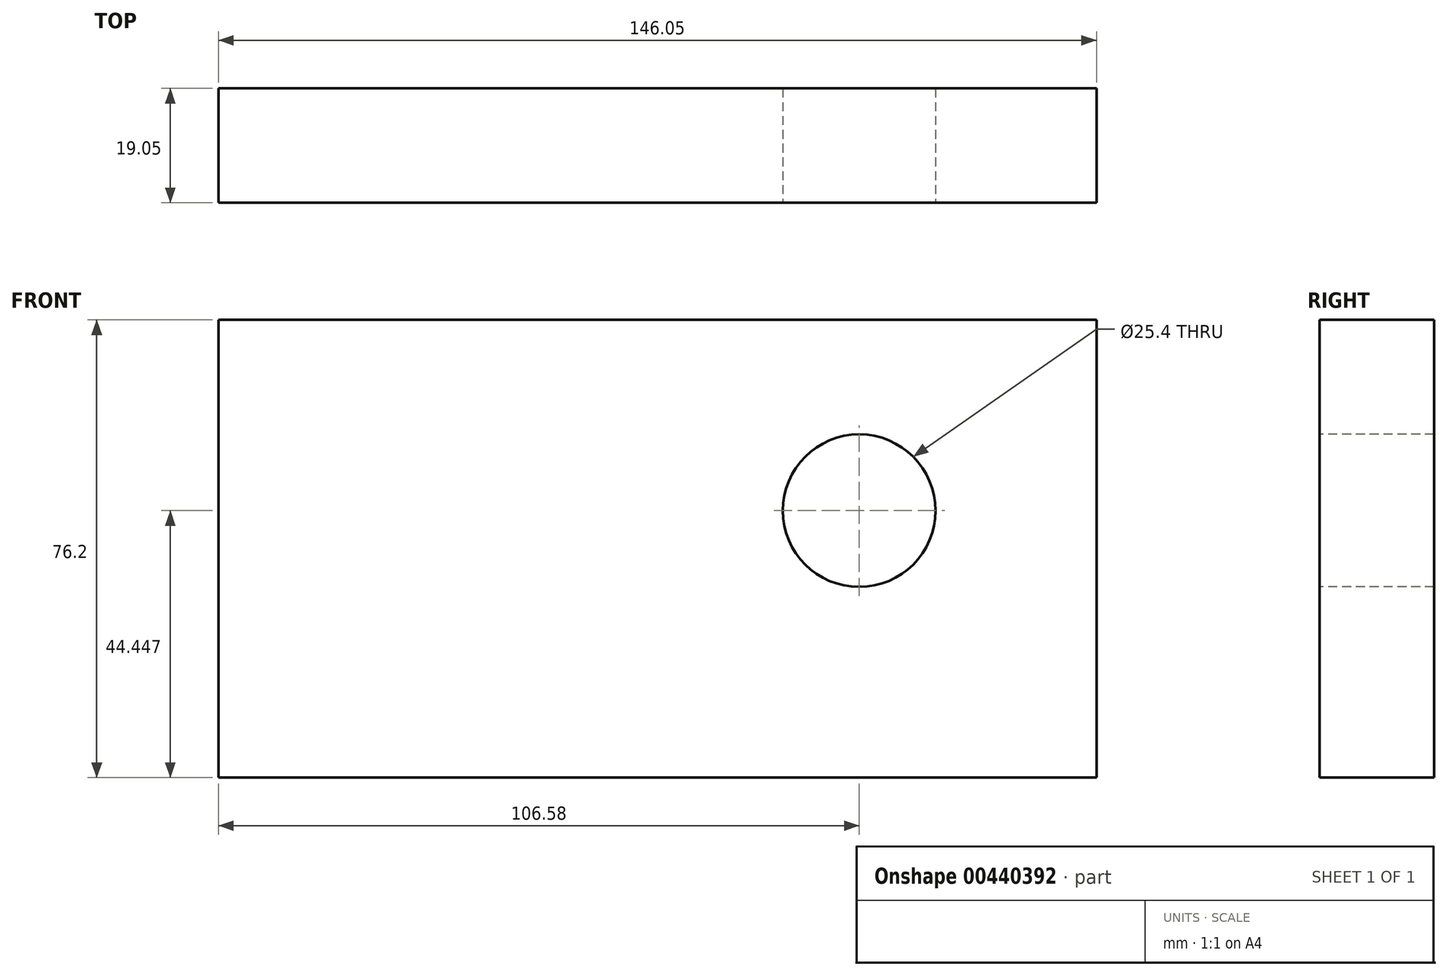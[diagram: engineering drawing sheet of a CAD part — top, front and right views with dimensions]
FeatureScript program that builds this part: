
annotation { "Feature Type Name" : "Feature", "Feature Type Description" : "" }
export const myFeature = defineFeature(function(context is Context, id is Id, definition is map)
    precondition{}
    {
        {
            var Q0;
            Q0=qCreatedBy(makeId("Front.planeOp"),FACE);
            var sketch = newSketch(context, id + "F0", { "sketchPlane" : qUnion([Q0])});
            skLineSegment(sketch, "E0.bottom", {"start": v(-106.58, 69.18) * mm, "end": v(39.47, 69.18) * mm});
            skLineSegment(sketch, "E0.top", {"start": v(-106.58, -7.02) * mm, "end": v(39.47, -7.02) * mm});
            skLineSegment(sketch, "E0.left", {"start": v(-106.58, 69.18) * mm, "end": v(-106.58, -7.02) * mm});
            skLineSegment(sketch, "E0.right", {"start": v(39.47, 69.18) * mm, "end": v(39.47, -7.02) * mm});
            skSolve(sketch);
        }
        {
            var Q0;
            Q0 = qSketchRegion(id + "F0", true);
            extrude(context, id + "F1", {"entities" : qUnion([Q0]), "depth" : 19.05 * mm});
        }
        {
            var Q0;
            Q0=makeQuery(id+"F1.opExtrude","CAP_FACE",FACE,{"disambiguationData":[OSD([sQuery(id+"F0.wireOp",EDGE,"E0.bottom"),sQuery(id+"F0.wireOp",EDGE,"E0.top"),sQuery(id+"F0.wireOp",EDGE,"E0.left"),sQuery(id+"F0.wireOp",EDGE,"E0.right")])],"isStart":false});
            var sketch = newSketch(context, id + "F2", { "sketchPlane" : qUnion([Q0])});
            skLineSegment(sketch, "E1.bottom", {"start": v(-92.75, 56.48) * mm, "end": v(-67.35, 56.48) * mm});
            skLineSegment(sketch, "E1.top", {"start": v(-92.75, 31.08) * mm, "end": v(-67.35, 31.08) * mm});
            skLineSegment(sketch, "E1.left", {"start": v(-92.75, 56.48) * mm, "end": v(-92.75, 31.08) * mm});
            skLineSegment(sketch, "E1.right", {"start": v(-67.35, 56.48) * mm, "end": v(-67.35, 31.08) * mm});
            skCircle(sketch, "E2", {"center": v(0, 37.43) * mm, "radius": 12.7 * mm});
            skSolve(sketch);
        }
        {
            var Q0;
            Q0=makeQuery(id+"F2.imprint","IMPRINT",FACE,{"disambiguationData":[TD([[makeQuery(id+"F2.imprint","IMPRINT",EDGE,{"derivedFrom":sQuery(id+"F2.wireOp",EDGE,"E2")}),1.0]])]});
            extrude(context, id + "F3", {"entities" : qUnion([Q0]), "operationType" : NewBodyOperationType.REMOVE, "oppositeDirection" : true, "depth" : 25.4 * mm, "offsetDistance" : 25.4 * mm});
        }
    });
